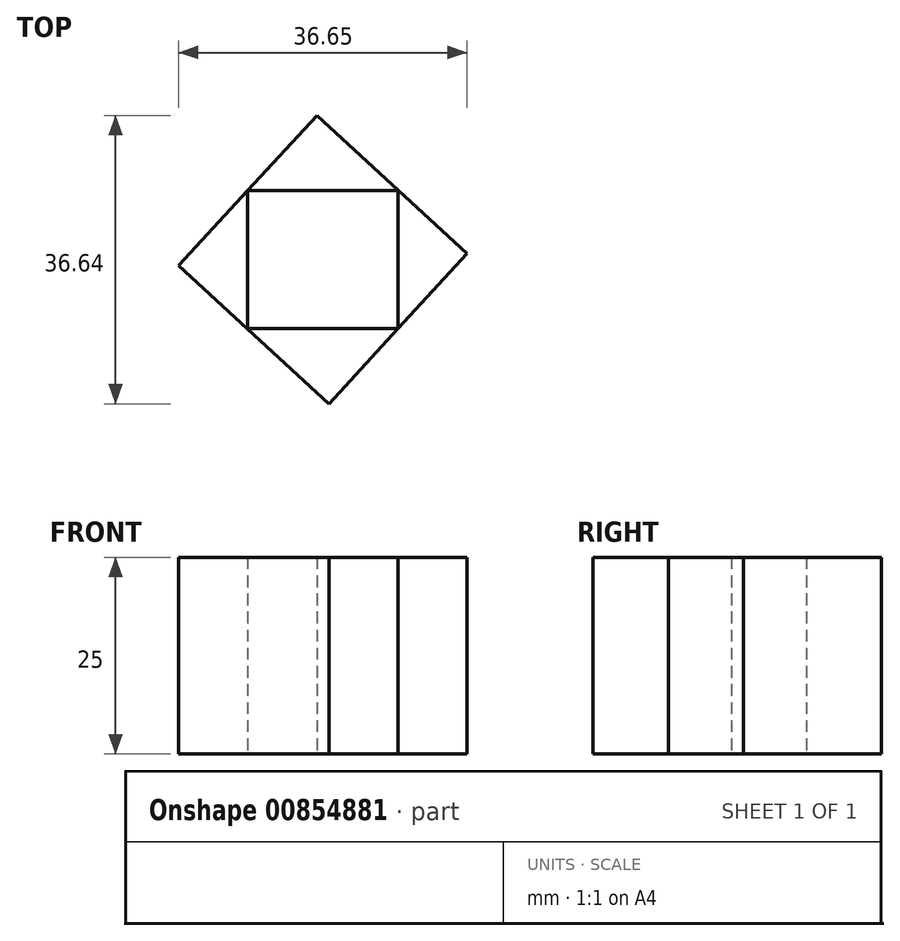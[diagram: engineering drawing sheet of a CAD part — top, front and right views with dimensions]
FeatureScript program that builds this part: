
annotation { "Feature Type Name" : "Feature", "Feature Type Description" : "" }
export const myFeature = defineFeature(function(context is Context, id is Id, definition is map)
    precondition{}
    {
        {
            var Q0;
            Q0=qCreatedBy(makeId("Top.planeOp"),FACE);
            var sketch = newSketch(context, id + "F0", { "sketchPlane" : qUnion([Q0])});
            skLineSegment(sketch, "E0.bottom", {"start": v(-34.4, 25.56) * mm, "end": v(-15.32, 25.56) * mm});
            skLineSegment(sketch, "E0.top", {"start": v(-34.4, 8) * mm, "end": v(-15.32, 8) * mm});
            skLineSegment(sketch, "E0.left", {"start": v(-34.4, 25.56) * mm, "end": v(-34.4, 8) * mm});
            skLineSegment(sketch, "E0.right", {"start": v(-15.32, 25.56) * mm, "end": v(-15.32, 8) * mm});
            skLineSegment(sketch, "E1.0", {"start": v(-6.54, 17.55) * mm, "end": v(-24.1, -1.54) * mm});
            skLineSegment(sketch, "E1.1", {"start": v(-24.1, -1.54) * mm, "end": v(-43.19, 16.01) * mm});
            skLineSegment(sketch, "E1.2", {"start": v(-43.19, 16.01) * mm, "end": v(-25.63, 35.1) * mm});
            skLineSegment(sketch, "E1.3", {"start": v(-25.63, 35.1) * mm, "end": v(-6.54, 17.55) * mm});
            skPoint(sketch, "E1.0.midPoint", {"position": v(-15.32, 8) * mm});
            skSolve(sketch);
        }
        {
            var Q0;
            {var subQ4=sQuery(id+"F0.wireOp",EDGE,"E0.bottom");Q0=makeQuery(id+"F0.imprint","IMPRINT",FACE,{"disambiguationData":[TD([[makeQuery(id+"F0.imprint","IMPRINT",EDGE,{"derivedFrom":subQ4}),1.0]])]});}
            var Q1;
            {var subQ1=sQuery(id+"F0.wireOp",EDGE,"E0.top");Q1=makeQuery(id+"F0.imprint","IMPRINT",FACE,{"disambiguationData":[TD([[makeQuery(id+"F0.imprint","IMPRINT",EDGE,{"derivedFrom":subQ1}),-1.0]])]});}
            extrude(context, id + "F1", {"entities" : qUnion([Q0, Q1]), "depth" : 25 * mm, "offsetDistance" : 25 * mm});
        }
    });
